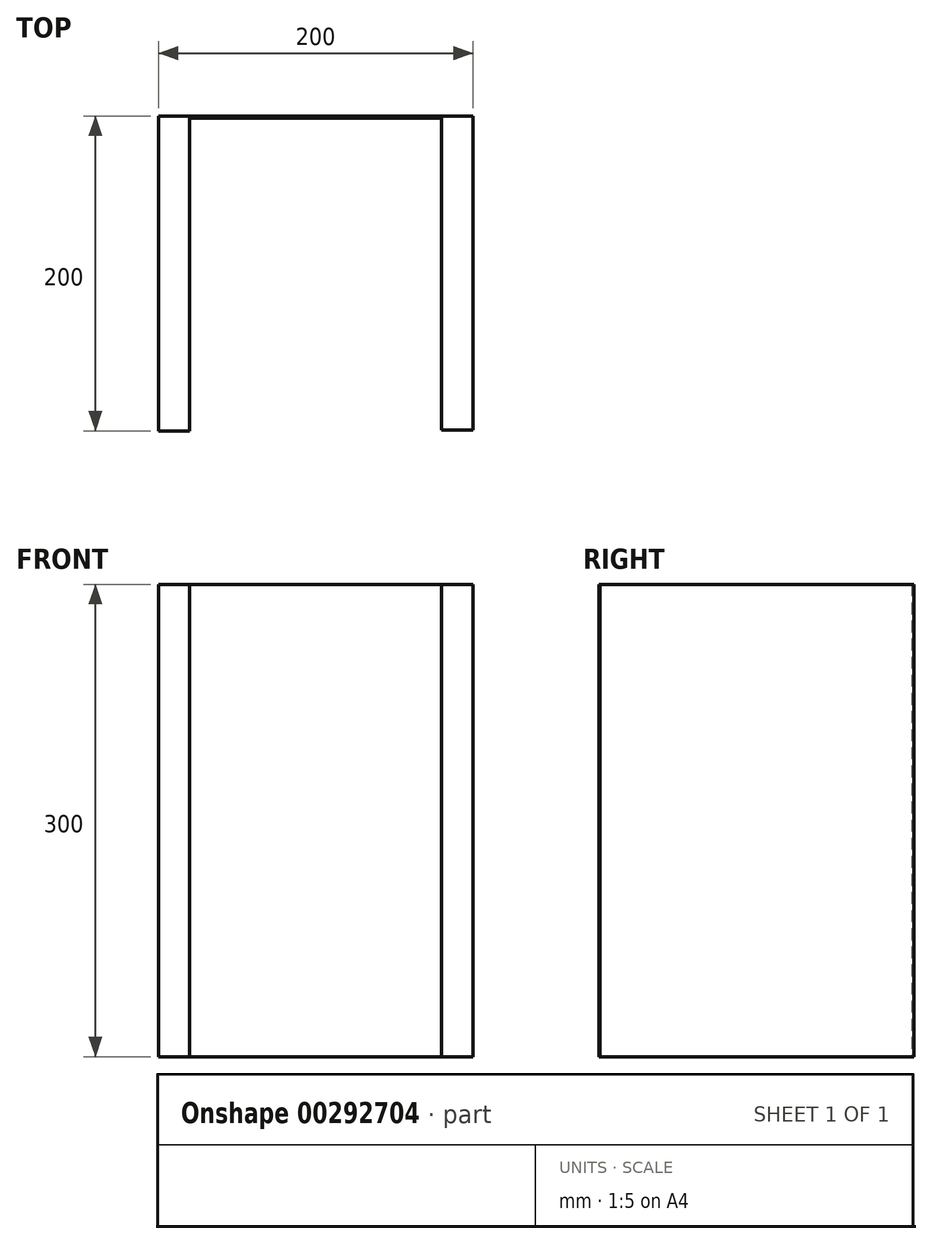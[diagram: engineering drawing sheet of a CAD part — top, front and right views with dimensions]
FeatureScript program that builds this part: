
annotation { "Feature Type Name" : "Feature", "Feature Type Description" : "" }
export const myFeature = defineFeature(function(context is Context, id is Id, definition is map)
    precondition{}
    {
        {
            var Q0;
            Q0=qCreatedBy(makeId("Front.planeOp"),FACE);
            var sketch = newSketch(context, id + "F0", { "sketchPlane" : qUnion([Q0])});
            skLineSegment(sketch, "E0.bottom", {"start": v(0, 300) * mm, "end": v(200, 300) * mm});
            skLineSegment(sketch, "E0.top", {"start": v(0, 0) * mm, "end": v(200, 0) * mm});
            skLineSegment(sketch, "E0.left", {"start": v(0, 300) * mm, "end": v(0, 0) * mm});
            skLineSegment(sketch, "E0.right", {"start": v(200, 300) * mm, "end": v(200, 0) * mm});
            skSolve(sketch);
        }
        {
            var Q0;
            Q0 = qSketchRegion(id + "F0", true);
            extrude(context, id + "F1", {"entities" : qUnion([Q0]), "depth" : 1.5 * mm});
        }
        {
            var Q0;
            Q0=qCreatedBy(makeId("Front.planeOp"),FACE);
            var sketch = newSketch(context, id + "F2", { "sketchPlane" : qUnion([Q0])});
            skLineSegment(sketch, "E1.bottom", {"start": v(0, 300) * mm, "end": v(20, 300) * mm});
            skLineSegment(sketch, "E1.top", {"start": v(0, 0) * mm, "end": v(20, 0) * mm});
            skLineSegment(sketch, "E1.left", {"start": v(20, 300) * mm, "end": v(20, 0) * mm});
            skLineSegment(sketch, "E1.right", {"start": v(0, 300) * mm, "end": v(0, 0) * mm});
            skSolve(sketch);
        }
        {
            var Q0;
            Q0 = qSketchRegion(id + "F2", true);
            extrude(context, id + "F3", {"entities" : qUnion([Q0]), "operationType" : NewBodyOperationType.ADD, "depth" : 200 * mm});
        }
        {
            var Q0;
            Q0=makeQuery(id+"F1.opExtrude","CAP_FACE",FACE,{"disambiguationData":[OSD([sQuery(id+"F0.wireOp",EDGE,"E0.bottom"),sQuery(id+"F0.wireOp",EDGE,"E0.top"),sQuery(id+"F0.wireOp",EDGE,"E0.left"),sQuery(id+"F0.wireOp",EDGE,"E0.right")])],"isStart":false});
            var sketch = newSketch(context, id + "F4", { "sketchPlane" : qUnion([Q0])});
            skLineSegment(sketch, "E2.bottom", {"start": v(200, 300) * mm, "end": v(180, 300) * mm});
            skLineSegment(sketch, "E2.top", {"start": v(200, 0) * mm, "end": v(180, 0) * mm});
            skLineSegment(sketch, "E2.left", {"start": v(200, 300) * mm, "end": v(200, 0) * mm});
            skLineSegment(sketch, "E2.right", {"start": v(180, 300) * mm, "end": v(180, 0) * mm});
            skSolve(sketch);
        }
        {
            var Q0;
            Q0 = qSketchRegion(id + "F4", true);
            extrude(context, id + "F5", {"entities" : qUnion([Q0]), "operationType" : NewBodyOperationType.ADD, "depth" : 198 * mm});
        }
    });
